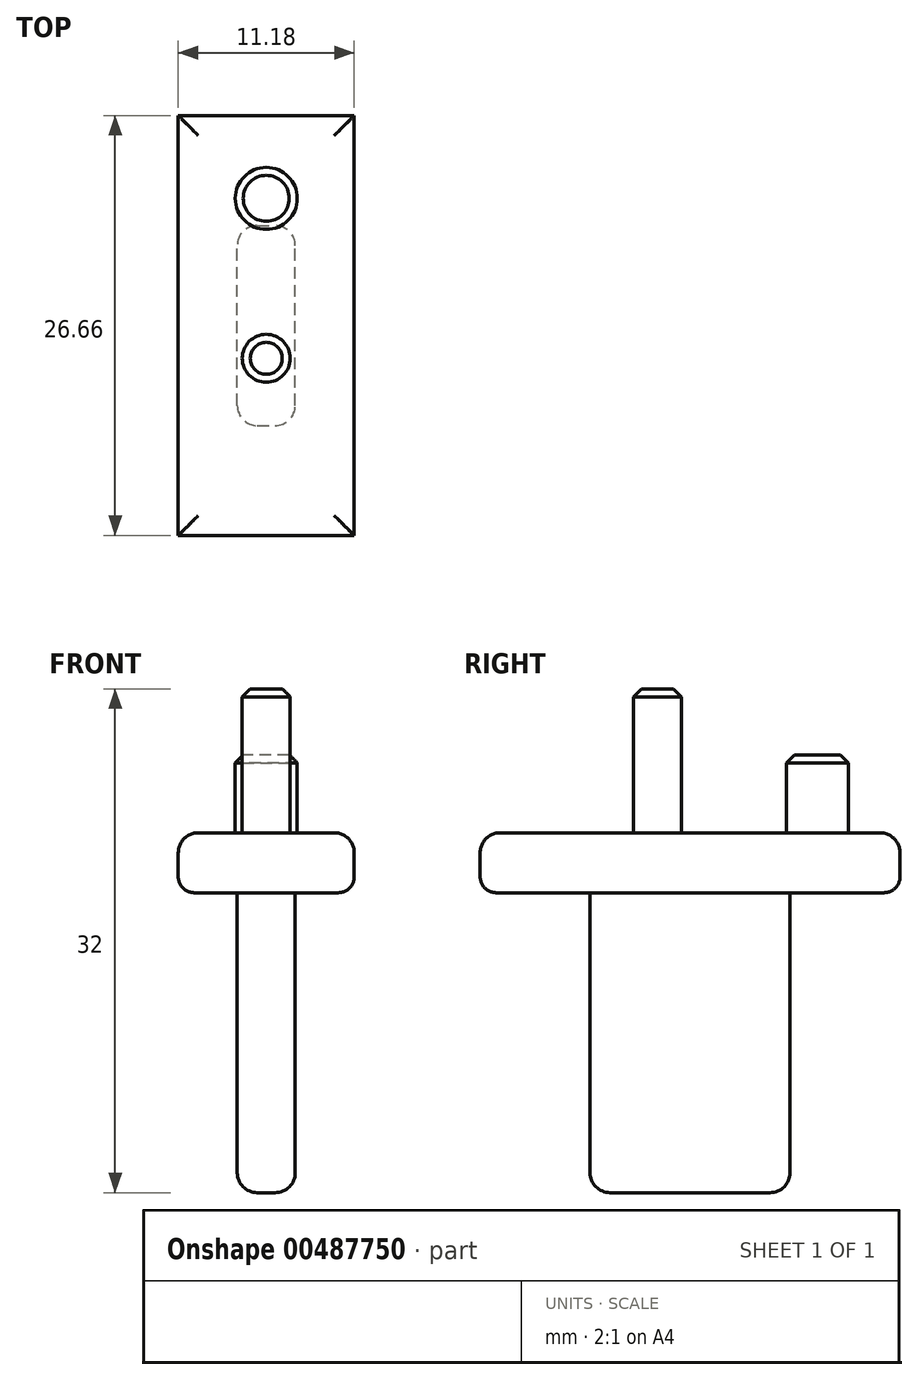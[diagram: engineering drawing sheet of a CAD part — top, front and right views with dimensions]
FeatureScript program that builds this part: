
annotation { "Feature Type Name" : "Feature", "Feature Type Description" : "" }
export const myFeature = defineFeature(function(context is Context, id is Id, definition is map)
    precondition{}
    {
        {
            var Q0;
            Q0=qCreatedBy(makeId("Top.planeOp"),FACE);
            var sketch = newSketch(context, id + "F0", { "sketchPlane" : qUnion([Q0])});
            skLineSegment(sketch, "E0.bottom", {"start": v(-5.59, 13.34) * mm, "end": v(5.59, 13.34) * mm});
            skLineSegment(sketch, "E0.top", {"start": v(-5.59, -13.34) * mm, "end": v(5.59, -13.34) * mm});
            skLineSegment(sketch, "E0.left", {"start": v(-5.59, 13.34) * mm, "end": v(-5.59, -13.34) * mm});
            skLineSegment(sketch, "E0.right", {"start": v(5.59, 13.33) * mm, "end": v(5.59, -13.34) * mm});
            skSolve(sketch);
        }
        {
            var Q0;
            Q0=makeQuery(id+"F0.imprint","IMPRINT",FACE,{"disambiguationData":[TD([[makeQuery(id+"F0.imprint","IMPRINT",EDGE,{"derivedFrom":sQuery(id+"F0.wireOp",EDGE,"E0.bottom")}),-1.0]])]});
            extrude(context, id + "F1", {"entities" : qUnion([Q0]), "depth" : 3.8 * mm});
        }
        {
            var Q0;
            Q0=makeQuery(id+"F1.opExtrude","CAP_FACE",FACE,{"disambiguationData":[OSD([sQuery(id+"F0.wireOp",EDGE,"E0.bottom"),sQuery(id+"F0.wireOp",EDGE,"E0.top"),sQuery(id+"F0.wireOp",EDGE,"E0.left"),sQuery(id+"F0.wireOp",EDGE,"E0.right")])],"isStart":false});
            var sketch = newSketch(context, id + "F2", { "sketchPlane" : qUnion([Q0])});
            skCircle(sketch, "E1", {"center": v(0, 8.08) * mm, "radius": 1.97 * mm});
            skCircle(sketch, "E2", {"center": v(0, -2.08) * mm, "radius": 1.52 * mm});
            skSolve(sketch);
        }
        {
            var Q0;
            Q0=makeQuery(id+"F2.imprint","IMPRINT",FACE,{"disambiguationData":[TD([[makeQuery(id+"F2.imprint","IMPRINT",EDGE,{"derivedFrom":sQuery(id+"F2.wireOp",EDGE,"E1")}),1.0]])]});
            extrude(context, id + "F3", {"entities" : qUnion([Q0]), "operationType" : NewBodyOperationType.ADD, "depth" : 4.95 * mm});
        }
        {
            var Q0;
            Q0=makeQuery(id+"F2.imprint","IMPRINT",FACE,{"disambiguationData":[TD([[makeQuery(id+"F2.imprint","IMPRINT",EDGE,{"derivedFrom":sQuery(id+"F2.wireOp",EDGE,"E2")}),1.0]])]});
            extrude(context, id + "F4", {"entities" : qUnion([Q0]), "operationType" : NewBodyOperationType.ADD, "depth" : 9.14 * mm});
        }
        {
            var Q0;
            Q0=makeQuery(id+"F3.opExtrude","CAP_EDGE",EDGE,{"disambiguationData":[OSD([sQuery(id+"F2.wireOp",EDGE,"E1")])],"isStart":false});
            var Q1;
            Q1=makeQuery(id+"F4.opExtrude","CAP_EDGE",EDGE,{"disambiguationData":[OSD([sQuery(id+"F2.wireOp",EDGE,"E2")])],"isStart":false});
            chamfer(context, id + "F5", {"entities" : qUnion([Q0, Q1]), "width" : 0.5 * mm, "tangentPropagation" : true});
        }
        {
            var Q0;
            Q0=makeQuery(id+"F1.opExtrude","CAP_EDGE",EDGE,{"disambiguationData":[OSD([sQuery(id+"F0.wireOp",EDGE,"E0.bottom")])],"isStart":false});
            var Q1;
            Q1=makeQuery(id+"F1.opExtrude","CAP_EDGE",EDGE,{"disambiguationData":[OSD([sQuery(id+"F0.wireOp",EDGE,"E0.right")])],"isStart":false});
            var Q2;
            Q2=makeQuery(id+"F1.opExtrude","CAP_EDGE",EDGE,{"disambiguationData":[OSD([sQuery(id+"F0.wireOp",EDGE,"E0.top")])],"isStart":false});
            var Q3;
            Q3=makeQuery(id+"F1.opExtrude","CAP_EDGE",EDGE,{"disambiguationData":[OSD([sQuery(id+"F0.wireOp",EDGE,"E0.left")])],"isStart":false});
            fillet(context, id + "F6", {"entities" : qUnion([Q0, Q1, Q2, Q3]), "radius" : 1.27 * mm, "tangentPropagation" : true, "allowEdgeOverflow" : false});
        }
        {
            var Q0;
            Q0=makeQuery(id+"F1.opExtrude","CAP_EDGE",EDGE,{"disambiguationData":[OSD([sQuery(id+"F0.wireOp",EDGE,"E0.bottom")])],"isStart":true});
            var Q1;
            Q1=makeQuery(id+"F1.opExtrude","CAP_EDGE",EDGE,{"disambiguationData":[OSD([sQuery(id+"F0.wireOp",EDGE,"E0.right")])],"isStart":true});
            var Q2;
            Q2=makeQuery(id+"F1.opExtrude","CAP_EDGE",EDGE,{"disambiguationData":[OSD([sQuery(id+"F0.wireOp",EDGE,"E0.top")])],"isStart":true});
            var Q3;
            Q3=makeQuery(id+"F1.opExtrude","CAP_EDGE",EDGE,{"disambiguationData":[OSD([sQuery(id+"F0.wireOp",EDGE,"E0.left")])],"isStart":true});
            fillet(context, id + "F7", {"entities" : qUnion([Q0, Q1, Q2, Q3]), "radius" : 1.02 * mm, "tangentPropagation" : true, "allowEdgeOverflow" : false});
        }
        {
            var Q0;
            Q0=makeQuery(id+"F1.opExtrude","CAP_FACE",FACE,{"disambiguationData":[OSD([sQuery(id+"F0.wireOp",EDGE,"E0.bottom"),sQuery(id+"F0.wireOp",EDGE,"E0.top"),sQuery(id+"F0.wireOp",EDGE,"E0.left"),sQuery(id+"F0.wireOp",EDGE,"E0.right")])],"isStart":true});
            var sketch = newSketch(context, id + "F8", { "sketchPlane" : qUnion([Q0])});
            skLineSegment(sketch, "E3.bottom", {"start": v(-1.84, 6.35) * mm, "end": v(1.84, 6.35) * mm});
            skLineSegment(sketch, "E3.top", {"start": v(-1.84, -6.35) * mm, "end": v(1.84, -6.35) * mm});
            skLineSegment(sketch, "E3.left", {"start": v(-1.84, 6.35) * mm, "end": v(-1.84, -6.35) * mm});
            skLineSegment(sketch, "E3.right", {"start": v(1.84, 6.35) * mm, "end": v(1.84, -6.35) * mm});
            skSolve(sketch);
        }
        {
            var Q0;
            Q0=makeQuery(id+"F8.imprint","IMPRINT",FACE,{"disambiguationData":[TD([[makeQuery(id+"F8.imprint","IMPRINT",EDGE,{"derivedFrom":sQuery(id+"F8.wireOp",EDGE,"E3.bottom")}),-1.0]])]});
            extrude(context, id + "F9", {"entities" : qUnion([Q0]), "operationType" : NewBodyOperationType.ADD, "depth" : 19.05 * mm});
        }
        {
            var Q0;
            Q0=makeQuery(id+"F9.opExtrude","CAP_EDGE",EDGE,{"disambiguationData":[OSD([sQuery(id+"F8.wireOp",EDGE,"E3.bottom")])],"isStart":false});
            var Q1;
            Q1=makeQuery(id+"F9.opExtrude","CAP_EDGE",EDGE,{"disambiguationData":[OSD([sQuery(id+"F8.wireOp",EDGE,"E3.left")])],"isStart":false});
            var Q2;
            Q2=makeQuery(id+"F9.opExtrude","CAP_EDGE",EDGE,{"disambiguationData":[OSD([sQuery(id+"F8.wireOp",EDGE,"E3.right")])],"isStart":false});
            var Q3;
            Q3=makeQuery(id+"F9.opExtrude","CAP_EDGE",EDGE,{"disambiguationData":[OSD([sQuery(id+"F8.wireOp",EDGE,"E3.top")])],"isStart":false});
            var Q4;
            Q4=makeQuery(id+"F9.opExtrude","SWEPT_EDGE",EDGE,{"disambiguationData":[OSD([sQuery(id+"F8.wireOp",EDGE,"E3.bottom"),sQuery(id+"F8.wireOp",EDGE,"E3.left")])]});
            var Q5;
            Q5=makeQuery(id+"F9.opExtrude","SWEPT_EDGE",EDGE,{"disambiguationData":[OSD([sQuery(id+"F8.wireOp",EDGE,"E3.bottom"),sQuery(id+"F8.wireOp",EDGE,"E3.right")])]});
            var Q6;
            Q6=makeQuery(id+"F9.opExtrude","SWEPT_EDGE",EDGE,{"disambiguationData":[OSD([sQuery(id+"F8.wireOp",EDGE,"E3.top"),sQuery(id+"F8.wireOp",EDGE,"E3.right")])]});
            var Q7;
            Q7=makeQuery(id+"F9.opExtrude","SWEPT_EDGE",EDGE,{"disambiguationData":[OSD([sQuery(id+"F8.wireOp",EDGE,"E3.top"),sQuery(id+"F8.wireOp",EDGE,"E3.left")])]});
            fillet(context, id + "F10", {"entities" : qUnion([Q0, Q1, Q2, Q3, Q4, Q5, Q6, Q7]), "radius" : 1.27 * mm, "tangentPropagation" : true, "allowEdgeOverflow" : false});
        }
    });
